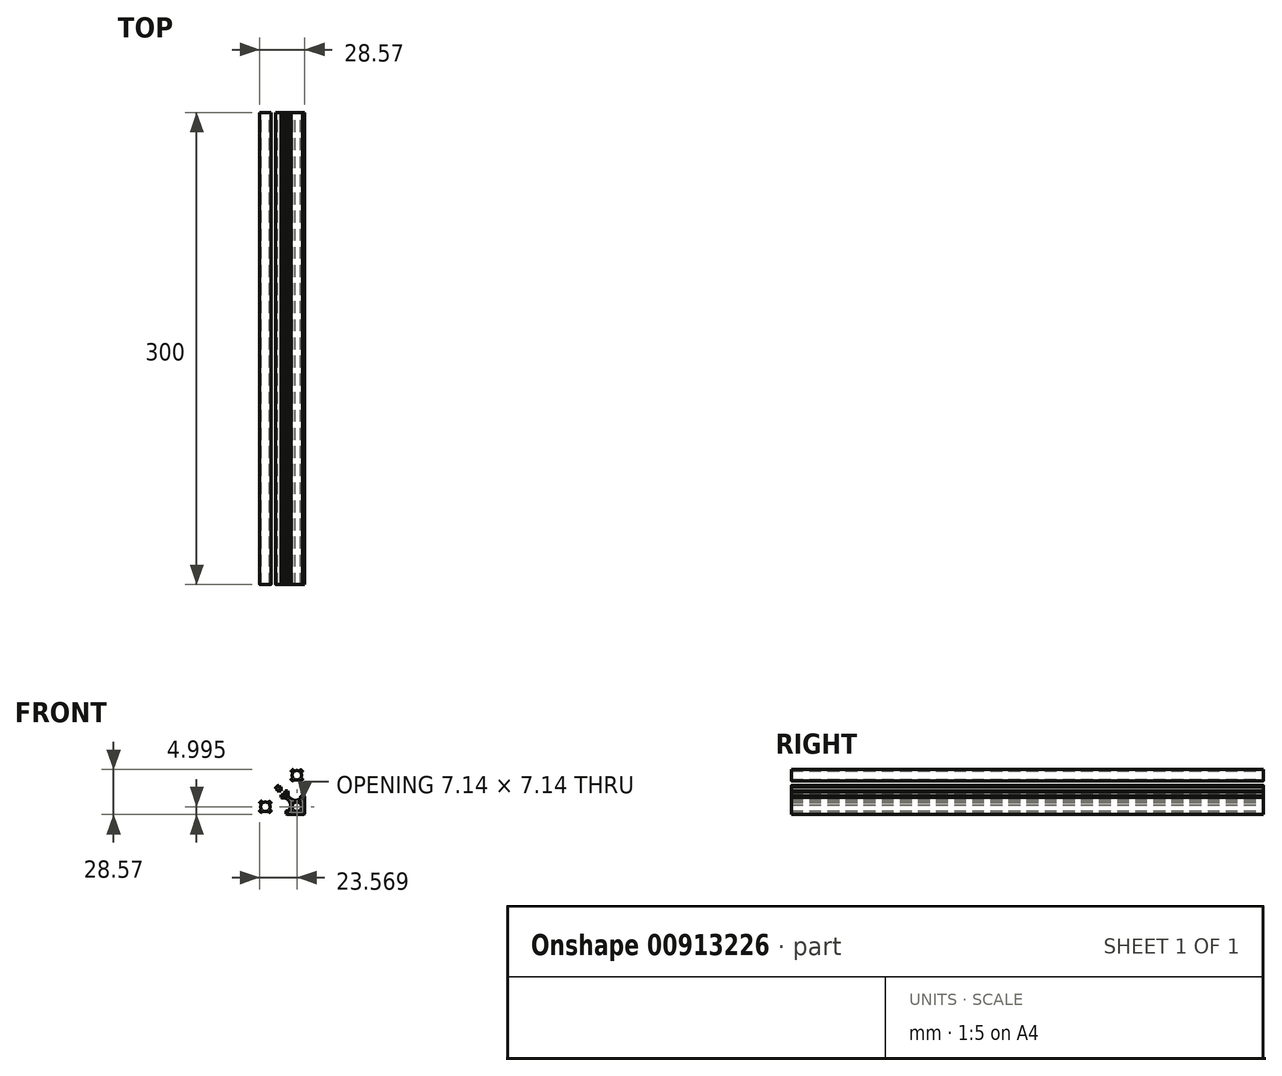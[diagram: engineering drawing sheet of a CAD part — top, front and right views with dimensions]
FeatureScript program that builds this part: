
annotation { "Feature Type Name" : "Feature", "Feature Type Description" : "" }
export const myFeature = defineFeature(function(context is Context, id is Id, definition is map)
    precondition{}
    {
        {
            var Q0;
            Q0=qCreatedBy(makeId("Front.planeOp"),FACE);
            var sketch = newSketch(context, id + "F0", { "sketchPlane" : qUnion([Q0])});
            skLineSegment(sketch, "E0", {"start": v(-2.82, -20.25) * mm, "end": v(-2.82, -15.85) * mm});
            skLineSegment(sketch, "E1", {"start": v(-5.02, -18.05) * mm, "end": v(-0.62, -18.05) * mm});
            skArc(sketch, "E2", {"start": v(-5.5, -19.39) * mm, "mid": v(-5.48, -19.57) * mm, "end": v(-5.56, -19.74) * mm});
            skLineSegment(sketch, "E3", {"start": v(-5.56, -19.74) * mm, "end": v(-6.3, -20.48) * mm});
            skArc(sketch, "E4", {"start": v(-6.3, -20.48) * mm, "mid": v(-6.4, -20.67) * mm, "end": v(-6.32, -20.88) * mm});
            skArc(sketch, "E5", {"start": v(-6.32, -20.88) * mm, "mid": v(-6, -21.24) * mm, "end": v(-5.64, -21.56) * mm});
            skArc(sketch, "E6", {"start": v(-5.64, -21.56) * mm, "mid": v(-5.44, -21.62) * mm, "end": v(-5.24, -21.54) * mm});
            skLineSegment(sketch, "E7", {"start": v(-5.24, -21.54) * mm, "end": v(-4.5, -20.8) * mm});
            skArc(sketch, "E8", {"start": v(-4.5, -20.8) * mm, "mid": v(-4.34, -20.71) * mm, "end": v(-4.16, -20.74) * mm});
            skArc(sketch, "E9", {"start": v(-4.16, -20.74) * mm, "mid": v(-2.82, -21.05) * mm, "end": v(-1.48, -20.74) * mm});
            skArc(sketch, "E10", {"start": v(-1.48, -20.74) * mm, "mid": v(-1.3, -20.71) * mm, "end": v(-1.14, -20.8) * mm});
            skLineSegment(sketch, "E11", {"start": v(-1.14, -20.8) * mm, "end": v(-0.4, -21.54) * mm});
            skArc(sketch, "E12", {"start": v(-0.4, -21.54) * mm, "mid": v(-0.2, -21.62) * mm, "end": v(0, -21.56) * mm});
            skArc(sketch, "E13", {"start": v(0, -21.56) * mm, "mid": v(0.36, -21.24) * mm, "end": v(0.68, -20.88) * mm});
            skArc(sketch, "E14", {"start": v(0.68, -20.88) * mm, "mid": v(0.75, -20.67) * mm, "end": v(0.66, -20.48) * mm});
            skLineSegment(sketch, "E15", {"start": v(0.66, -20.48) * mm, "end": v(-0.08, -19.74) * mm});
            skArc(sketch, "E16", {"start": v(-0.08, -19.74) * mm, "mid": v(-0.16, -19.57) * mm, "end": v(-0.13, -19.39) * mm});
            skArc(sketch, "E17", {"start": v(-0.13, -19.39) * mm, "mid": v(0.18, -18.05) * mm, "end": v(-0.13, -16.72) * mm});
            skArc(sketch, "E18", {"start": v(-0.13, -16.72) * mm, "mid": v(-0.16, -16.54) * mm, "end": v(-0.08, -16.37) * mm});
            skLineSegment(sketch, "E19", {"start": v(-0.08, -16.37) * mm, "end": v(0.66, -15.63) * mm});
            skArc(sketch, "E20", {"start": v(0.66, -15.63) * mm, "mid": v(0.75, -15.44) * mm, "end": v(0.68, -15.23) * mm});
            skArc(sketch, "E21", {"start": v(0.68, -15.23) * mm, "mid": v(0.36, -14.87) * mm, "end": v(0, -14.55) * mm});
            skArc(sketch, "E22", {"start": v(0, -14.55) * mm, "mid": v(-0.2, -14.48) * mm, "end": v(-0.4, -14.57) * mm});
            skLineSegment(sketch, "E23", {"start": v(-0.4, -14.57) * mm, "end": v(-1.14, -15.31) * mm});
            skArc(sketch, "E24", {"start": v(-1.14, -15.31) * mm, "mid": v(-1.3, -15.4) * mm, "end": v(-1.48, -15.37) * mm});
            skArc(sketch, "E25", {"start": v(-1.48, -15.37) * mm, "mid": v(-2.82, -15.05) * mm, "end": v(-4.16, -15.37) * mm});
            skArc(sketch, "E26", {"start": v(-4.16, -15.37) * mm, "mid": v(-4.34, -15.4) * mm, "end": v(-4.5, -15.31) * mm});
            skLineSegment(sketch, "E27", {"start": v(-4.5, -15.31) * mm, "end": v(-5.24, -14.57) * mm});
            skArc(sketch, "E28", {"start": v(-5.24, -14.57) * mm, "mid": v(-5.44, -14.48) * mm, "end": v(-5.64, -14.55) * mm});
            skArc(sketch, "E29", {"start": v(-5.64, -14.55) * mm, "mid": v(-6, -14.87) * mm, "end": v(-6.32, -15.23) * mm});
            skArc(sketch, "E30", {"start": v(-6.32, -15.23) * mm, "mid": v(-6.4, -15.44) * mm, "end": v(-6.3, -15.63) * mm});
            skLineSegment(sketch, "E31", {"start": v(-6.3, -15.63) * mm, "end": v(-5.56, -16.37) * mm});
            skArc(sketch, "E32", {"start": v(-5.56, -16.37) * mm, "mid": v(-5.48, -16.54) * mm, "end": v(-5.5, -16.72) * mm});
            skArc(sketch, "E33", {"start": v(-5.5, -16.72) * mm, "mid": v(-5.82, -18.05) * mm, "end": v(-5.5, -19.39) * mm});
            skLineSegment(sketch, "E34", {"start": v(-5.02, -38.05) * mm, "end": v(-0.62, -38.05) * mm});
            skLineSegment(sketch, "E35", {"start": v(-2.82, -35.85) * mm, "end": v(-2.82, -40.25) * mm});
            skArc(sketch, "E36", {"start": v(-5.5, -36.72) * mm, "mid": v(-5.48, -36.54) * mm, "end": v(-5.56, -36.37) * mm});
            skLineSegment(sketch, "E37", {"start": v(-5.56, -36.37) * mm, "end": v(-6.3, -35.63) * mm});
            skArc(sketch, "E38", {"start": v(-6.3, -35.63) * mm, "mid": v(-6.4, -35.44) * mm, "end": v(-6.33, -35.23) * mm});
            skArc(sketch, "E39", {"start": v(-6.33, -35.23) * mm, "mid": v(-6, -34.87) * mm, "end": v(-5.64, -34.55) * mm});
            skArc(sketch, "E40", {"start": v(-5.64, -34.55) * mm, "mid": v(-5.44, -34.48) * mm, "end": v(-5.24, -34.57) * mm});
            skLineSegment(sketch, "E41", {"start": v(-5.24, -34.57) * mm, "end": v(-4.5, -35.31) * mm});
            skArc(sketch, "E42", {"start": v(-4.5, -35.31) * mm, "mid": v(-4.34, -35.4) * mm, "end": v(-4.16, -35.37) * mm});
            skArc(sketch, "E43", {"start": v(-4.16, -35.37) * mm, "mid": v(-2.82, -35.05) * mm, "end": v(-1.48, -35.37) * mm});
            skArc(sketch, "E44", {"start": v(-1.48, -35.37) * mm, "mid": v(-1.3, -35.4) * mm, "end": v(-1.14, -35.31) * mm});
            skLineSegment(sketch, "E45", {"start": v(-1.14, -35.31) * mm, "end": v(-0.4, -34.57) * mm});
            skArc(sketch, "E46", {"start": v(-0.4, -34.57) * mm, "mid": v(-0.2, -34.48) * mm, "end": v(0, -34.55) * mm});
            skArc(sketch, "E47", {"start": v(0, -34.55) * mm, "mid": v(0.36, -34.87) * mm, "end": v(0.68, -35.23) * mm});
            skArc(sketch, "E48", {"start": v(0.68, -35.23) * mm, "mid": v(0.75, -35.44) * mm, "end": v(0.66, -35.63) * mm});
            skLineSegment(sketch, "E49", {"start": v(0.66, -35.63) * mm, "end": v(-0.08, -36.37) * mm});
            skArc(sketch, "E50", {"start": v(-0.08, -36.37) * mm, "mid": v(-0.16, -36.54) * mm, "end": v(-0.13, -36.72) * mm});
            skArc(sketch, "E51", {"start": v(-0.13, -36.72) * mm, "mid": v(0.18, -38.05) * mm, "end": v(-0.14, -39.4) * mm});
            skArc(sketch, "E52", {"start": v(-0.14, -39.4) * mm, "mid": v(-0.16, -39.57) * mm, "end": v(-0.08, -39.74) * mm});
            skLineSegment(sketch, "E53", {"start": v(-0.08, -39.74) * mm, "end": v(0.66, -40.48) * mm});
            skArc(sketch, "E54", {"start": v(0.66, -40.48) * mm, "mid": v(0.75, -40.67) * mm, "end": v(0.68, -40.88) * mm});
            skArc(sketch, "E55", {"start": v(0.68, -40.88) * mm, "mid": v(0.36, -41.24) * mm, "end": v(0, -41.56) * mm});
            skArc(sketch, "E56", {"start": v(0, -41.56) * mm, "mid": v(-0.2, -41.63) * mm, "end": v(-0.4, -41.54) * mm});
            skLineSegment(sketch, "E57", {"start": v(-0.4, -41.54) * mm, "end": v(-1.14, -40.8) * mm});
            skArc(sketch, "E58", {"start": v(-1.14, -40.8) * mm, "mid": v(-1.3, -40.71) * mm, "end": v(-1.49, -40.74) * mm});
            skArc(sketch, "E59", {"start": v(-1.49, -40.74) * mm, "mid": v(-2.82, -41.05) * mm, "end": v(-4.16, -40.74) * mm});
            skArc(sketch, "E60", {"start": v(-4.16, -40.74) * mm, "mid": v(-4.34, -40.71) * mm, "end": v(-4.5, -40.8) * mm});
            skLineSegment(sketch, "E61", {"start": v(-4.5, -40.8) * mm, "end": v(-5.24, -41.54) * mm});
            skArc(sketch, "E62", {"start": v(-5.24, -41.54) * mm, "mid": v(-5.44, -41.62) * mm, "end": v(-5.64, -41.56) * mm});
            skArc(sketch, "E63", {"start": v(-5.64, -41.56) * mm, "mid": v(-6, -41.24) * mm, "end": v(-6.33, -40.88) * mm});
            skArc(sketch, "E64", {"start": v(-6.33, -40.88) * mm, "mid": v(-6.4, -40.67) * mm, "end": v(-6.3, -40.48) * mm});
            skLineSegment(sketch, "E65", {"start": v(-6.3, -40.48) * mm, "end": v(-5.56, -39.74) * mm});
            skArc(sketch, "E66", {"start": v(-5.56, -39.74) * mm, "mid": v(-5.48, -39.57) * mm, "end": v(-5.5, -39.4) * mm});
            skArc(sketch, "E67", {"start": v(-5.5, -39.4) * mm, "mid": v(-5.82, -38.05) * mm, "end": v(-5.5, -36.72) * mm});
            skArc(sketch, "E68", {"start": v(-20.13, -36.72) * mm, "mid": v(-20.16, -36.54) * mm, "end": v(-20.07, -36.37) * mm});
            skLineSegment(sketch, "E69", {"start": v(-20.07, -36.37) * mm, "end": v(-19.33, -35.63) * mm});
            skArc(sketch, "E70", {"start": v(-19.33, -35.63) * mm, "mid": v(-19.25, -35.44) * mm, "end": v(-19.31, -35.23) * mm});
            skArc(sketch, "E71", {"start": v(-19.31, -35.23) * mm, "mid": v(-19.64, -34.87) * mm, "end": v(-20, -34.55) * mm});
            skArc(sketch, "E72", {"start": v(-20, -34.55) * mm, "mid": v(-20.2, -34.48) * mm, "end": v(-20.4, -34.57) * mm});
            skLineSegment(sketch, "E73", {"start": v(-20.4, -34.57) * mm, "end": v(-21.14, -35.31) * mm});
            skArc(sketch, "E74", {"start": v(-21.14, -35.31) * mm, "mid": v(-21.3, -35.4) * mm, "end": v(-21.48, -35.37) * mm});
            skArc(sketch, "E75", {"start": v(-21.48, -35.37) * mm, "mid": v(-22.82, -35.05) * mm, "end": v(-24.15, -35.37) * mm});
            skArc(sketch, "E76", {"start": v(-24.15, -35.37) * mm, "mid": v(-24.34, -35.4) * mm, "end": v(-24.5, -35.31) * mm});
            skLineSegment(sketch, "E77", {"start": v(-24.5, -35.31) * mm, "end": v(-25.24, -34.57) * mm});
            skArc(sketch, "E78", {"start": v(-25.24, -34.57) * mm, "mid": v(-25.44, -34.48) * mm, "end": v(-25.64, -34.55) * mm});
            skArc(sketch, "E79", {"start": v(-25.64, -34.55) * mm, "mid": v(-26, -34.87) * mm, "end": v(-26.32, -35.23) * mm});
            skArc(sketch, "E80", {"start": v(-26.32, -35.23) * mm, "mid": v(-26.39, -35.44) * mm, "end": v(-26.3, -35.63) * mm});
            skLineSegment(sketch, "E81", {"start": v(-26.3, -35.63) * mm, "end": v(-25.56, -36.37) * mm});
            skArc(sketch, "E82", {"start": v(-25.56, -36.37) * mm, "mid": v(-25.48, -36.54) * mm, "end": v(-25.5, -36.72) * mm});
            skArc(sketch, "E83", {"start": v(-25.5, -36.72) * mm, "mid": v(-25.82, -38.05) * mm, "end": v(-25.5, -39.4) * mm});
            skArc(sketch, "E84", {"start": v(-25.5, -39.4) * mm, "mid": v(-25.48, -39.57) * mm, "end": v(-25.56, -39.74) * mm});
            skLineSegment(sketch, "E85", {"start": v(-25.56, -39.74) * mm, "end": v(-26.3, -40.48) * mm});
            skArc(sketch, "E86", {"start": v(-26.3, -40.48) * mm, "mid": v(-26.39, -40.67) * mm, "end": v(-26.32, -40.88) * mm});
            skArc(sketch, "E87", {"start": v(-26.32, -40.88) * mm, "mid": v(-26, -41.24) * mm, "end": v(-25.64, -41.56) * mm});
            skArc(sketch, "E88", {"start": v(-25.64, -41.56) * mm, "mid": v(-25.44, -41.63) * mm, "end": v(-25.24, -41.54) * mm});
            skLineSegment(sketch, "E89", {"start": v(-25.24, -41.54) * mm, "end": v(-24.5, -40.8) * mm});
            skArc(sketch, "E90", {"start": v(-24.5, -40.8) * mm, "mid": v(-24.33, -40.71) * mm, "end": v(-24.15, -40.74) * mm});
            skArc(sketch, "E91", {"start": v(-24.15, -40.74) * mm, "mid": v(-22.82, -41.05) * mm, "end": v(-21.48, -40.74) * mm});
            skArc(sketch, "E92", {"start": v(-21.48, -40.74) * mm, "mid": v(-21.3, -40.71) * mm, "end": v(-21.14, -40.8) * mm});
            skLineSegment(sketch, "E93", {"start": v(-21.14, -40.8) * mm, "end": v(-20.4, -41.54) * mm});
            skArc(sketch, "E94", {"start": v(-20.4, -41.54) * mm, "mid": v(-20.2, -41.62) * mm, "end": v(-20, -41.56) * mm});
            skArc(sketch, "E95", {"start": v(-20, -41.56) * mm, "mid": v(-19.63, -41.24) * mm, "end": v(-19.31, -40.88) * mm});
            skArc(sketch, "E96", {"start": v(-19.31, -40.88) * mm, "mid": v(-19.25, -40.67) * mm, "end": v(-19.33, -40.48) * mm});
            skLineSegment(sketch, "E97", {"start": v(-19.33, -40.48) * mm, "end": v(-20.07, -39.74) * mm});
            skArc(sketch, "E98", {"start": v(-20.07, -39.74) * mm, "mid": v(-20.16, -39.57) * mm, "end": v(-20.13, -39.4) * mm});
            skArc(sketch, "E99", {"start": v(-20.13, -39.4) * mm, "mid": v(-19.82, -38.05) * mm, "end": v(-20.13, -36.72) * mm});
            skLineSegment(sketch, "E100", {"start": v(-22.82, -35.85) * mm, "end": v(-22.82, -40.25) * mm});
            skLineSegment(sketch, "E101", {"start": v(-20.62, -38.05) * mm, "end": v(-25.02, -38.05) * mm});
            skLineSegment(sketch, "E102", {"start": v(-20.62, -18.05) * mm, "end": v(-25.02, -18.05) * mm});
            skLineSegment(sketch, "E103", {"start": v(-22.82, -20.25) * mm, "end": v(-22.82, -15.85) * mm});
            skLineSegment(sketch, "E104", {"start": v(2.64, -28.05) * mm, "end": v(-29.04, -28.05) * mm});
            skLineSegment(sketch, "E105", {"start": v(-12.82, -44) * mm, "end": v(-12.82, -12.06) * mm});
            skArc(sketch, "E106", {"start": v(-9.58, -26.47) * mm, "mid": v(-9.36, -26.3) * mm, "end": v(-9.38, -26.02) * mm});
            skArc(sketch, "E107", {"start": v(-9.38, -26.02) * mm, "mid": v(-10, -25.23) * mm, "end": v(-10.78, -24.61) * mm});
            skArc(sketch, "E108", {"start": v(-10.78, -24.61) * mm, "mid": v(-11.06, -24.6) * mm, "end": v(-11.23, -24.82) * mm});
            skLineSegment(sketch, "E109", {"start": v(-11.23, -24.82) * mm, "end": v(-11.37, -25.56) * mm});
            skArc(sketch, "E110", {"start": v(-11.37, -25.56) * mm, "mid": v(-11.52, -25.77) * mm, "end": v(-11.78, -25.78) * mm});
            skArc(sketch, "E111", {"start": v(-11.78, -25.78) * mm, "mid": v(-12.82, -25.55) * mm, "end": v(-13.85, -25.78) * mm});
            skArc(sketch, "E112", {"start": v(-13.85, -25.78) * mm, "mid": v(-14.11, -25.77) * mm, "end": v(-14.27, -25.56) * mm});
            skLineSegment(sketch, "E113", {"start": v(-14.27, -25.56) * mm, "end": v(-14.4, -24.82) * mm});
            skArc(sketch, "E114", {"start": v(-14.4, -24.82) * mm, "mid": v(-14.57, -24.6) * mm, "end": v(-14.85, -24.61) * mm});
            skArc(sketch, "E115", {"start": v(-14.85, -24.61) * mm, "mid": v(-15.65, -25.23) * mm, "end": v(-16.26, -26.02) * mm});
            skArc(sketch, "E116", {"start": v(-16.26, -26.02) * mm, "mid": v(-16.27, -26.3) * mm, "end": v(-16.06, -26.47) * mm});
            skLineSegment(sketch, "E117", {"start": v(-16.06, -26.47) * mm, "end": v(-15.31, -26.6) * mm});
            skArc(sketch, "E118", {"start": v(-15.31, -26.6) * mm, "mid": v(-15.1, -26.76) * mm, "end": v(-15.1, -27.02) * mm});
            skArc(sketch, "E119", {"start": v(-15.1, -27.02) * mm, "mid": v(-15.32, -28.05) * mm, "end": v(-15.1, -29.09) * mm});
            skArc(sketch, "E120", {"start": v(-15.1, -29.09) * mm, "mid": v(-15.1, -29.35) * mm, "end": v(-15.31, -29.5) * mm});
            skLineSegment(sketch, "E121", {"start": v(-15.31, -29.5) * mm, "end": v(-16.06, -29.64) * mm});
            skArc(sketch, "E122", {"start": v(-16.06, -29.64) * mm, "mid": v(-16.27, -29.81) * mm, "end": v(-16.26, -30.09) * mm});
            skArc(sketch, "E123", {"start": v(-16.26, -30.09) * mm, "mid": v(-15.65, -30.88) * mm, "end": v(-14.85, -31.5) * mm});
            skArc(sketch, "E124", {"start": v(-14.85, -31.5) * mm, "mid": v(-14.57, -31.51) * mm, "end": v(-14.4, -31.3) * mm});
            skLineSegment(sketch, "E125", {"start": v(-14.4, -31.3) * mm, "end": v(-14.27, -30.55) * mm});
            skArc(sketch, "E126", {"start": v(-14.27, -30.55) * mm, "mid": v(-14.11, -30.34) * mm, "end": v(-13.85, -30.33) * mm});
            skArc(sketch, "E127", {"start": v(-13.85, -30.33) * mm, "mid": v(-12.82, -30.55) * mm, "end": v(-11.78, -30.33) * mm});
            skArc(sketch, "E128", {"start": v(-11.78, -30.33) * mm, "mid": v(-11.52, -30.34) * mm, "end": v(-11.37, -30.55) * mm});
            skLineSegment(sketch, "E129", {"start": v(-11.37, -30.55) * mm, "end": v(-11.23, -31.3) * mm});
            skArc(sketch, "E130", {"start": v(-11.23, -31.3) * mm, "mid": v(-11.06, -31.51) * mm, "end": v(-10.78, -31.5) * mm});
            skArc(sketch, "E131", {"start": v(-10.78, -31.5) * mm, "mid": v(-10, -30.88) * mm, "end": v(-9.38, -30.09) * mm});
            skArc(sketch, "E132", {"start": v(-9.38, -30.09) * mm, "mid": v(-9.36, -29.81) * mm, "end": v(-9.58, -29.64) * mm});
            skLineSegment(sketch, "E133", {"start": v(-9.58, -29.64) * mm, "end": v(-10.32, -29.5) * mm});
            skArc(sketch, "E134", {"start": v(-10.32, -29.5) * mm, "mid": v(-10.53, -29.35) * mm, "end": v(-10.54, -29.09) * mm});
            skArc(sketch, "E135", {"start": v(-10.54, -29.09) * mm, "mid": v(-10.32, -28.05) * mm, "end": v(-10.54, -27.02) * mm});
            skArc(sketch, "E136", {"start": v(-10.54, -27.02) * mm, "mid": v(-10.53, -26.76) * mm, "end": v(-10.32, -26.6) * mm});
            skLineSegment(sketch, "E137", {"start": v(-10.32, -26.6) * mm, "end": v(-9.58, -26.47) * mm});
            skArc(sketch, "E138", {"start": v(-20.13, -19.39) * mm, "mid": v(-20.16, -19.57) * mm, "end": v(-20.08, -19.74) * mm});
            skLineSegment(sketch, "E139", {"start": v(-20.08, -19.74) * mm, "end": v(-19.33, -20.48) * mm});
            skArc(sketch, "E140", {"start": v(-19.33, -20.48) * mm, "mid": v(-19.25, -20.67) * mm, "end": v(-19.31, -20.88) * mm});
            skArc(sketch, "E141", {"start": v(-19.31, -20.88) * mm, "mid": v(-19.64, -21.24) * mm, "end": v(-20, -21.56) * mm});
            skArc(sketch, "E142", {"start": v(-20, -21.56) * mm, "mid": v(-20.2, -21.62) * mm, "end": v(-20.4, -21.54) * mm});
            skLineSegment(sketch, "E143", {"start": v(-20.4, -21.54) * mm, "end": v(-21.14, -20.8) * mm});
            skArc(sketch, "E144", {"start": v(-21.14, -20.8) * mm, "mid": v(-21.3, -20.71) * mm, "end": v(-21.48, -20.74) * mm});
            skArc(sketch, "E145", {"start": v(-21.48, -20.74) * mm, "mid": v(-22.82, -21.05) * mm, "end": v(-24.15, -20.74) * mm});
            skArc(sketch, "E146", {"start": v(-24.15, -20.74) * mm, "mid": v(-24.34, -20.71) * mm, "end": v(-24.5, -20.8) * mm});
            skLineSegment(sketch, "E147", {"start": v(-24.5, -20.8) * mm, "end": v(-25.24, -21.54) * mm});
            skArc(sketch, "E148", {"start": v(-25.24, -21.54) * mm, "mid": v(-25.44, -21.62) * mm, "end": v(-25.64, -21.56) * mm});
            skArc(sketch, "E149", {"start": v(-25.64, -21.56) * mm, "mid": v(-26, -21.24) * mm, "end": v(-26.32, -20.88) * mm});
            skArc(sketch, "E150", {"start": v(-26.32, -20.88) * mm, "mid": v(-26.39, -20.67) * mm, "end": v(-26.3, -20.48) * mm});
            skLineSegment(sketch, "E151", {"start": v(-26.3, -20.48) * mm, "end": v(-25.56, -19.74) * mm});
            skArc(sketch, "E152", {"start": v(-25.56, -19.74) * mm, "mid": v(-25.48, -19.57) * mm, "end": v(-25.5, -19.39) * mm});
            skArc(sketch, "E153", {"start": v(-25.5, -19.39) * mm, "mid": v(-25.82, -18.05) * mm, "end": v(-25.5, -16.72) * mm});
            skArc(sketch, "E154", {"start": v(-25.5, -16.72) * mm, "mid": v(-25.48, -16.54) * mm, "end": v(-25.56, -16.37) * mm});
            skLineSegment(sketch, "E155", {"start": v(-25.56, -16.37) * mm, "end": v(-26.3, -15.63) * mm});
            skArc(sketch, "E156", {"start": v(-26.3, -15.63) * mm, "mid": v(-26.39, -15.44) * mm, "end": v(-26.32, -15.23) * mm});
            skArc(sketch, "E157", {"start": v(-26.32, -15.23) * mm, "mid": v(-26, -14.87) * mm, "end": v(-25.64, -14.55) * mm});
            skArc(sketch, "E158", {"start": v(-25.64, -14.55) * mm, "mid": v(-25.44, -14.48) * mm, "end": v(-25.24, -14.57) * mm});
            skLineSegment(sketch, "E159", {"start": v(-25.24, -14.57) * mm, "end": v(-24.5, -15.31) * mm});
            skArc(sketch, "E160", {"start": v(-24.5, -15.31) * mm, "mid": v(-24.34, -15.4) * mm, "end": v(-24.15, -15.37) * mm});
            skArc(sketch, "E161", {"start": v(-24.15, -15.37) * mm, "mid": v(-22.82, -15.05) * mm, "end": v(-21.48, -15.37) * mm});
            skArc(sketch, "E162", {"start": v(-21.48, -15.37) * mm, "mid": v(-21.3, -15.4) * mm, "end": v(-21.14, -15.31) * mm});
            skLineSegment(sketch, "E163", {"start": v(-21.14, -15.31) * mm, "end": v(-20.4, -14.57) * mm});
            skArc(sketch, "E164", {"start": v(-20.4, -14.57) * mm, "mid": v(-20.2, -14.48) * mm, "end": v(-20, -14.55) * mm});
            skArc(sketch, "E165", {"start": v(-20, -14.55) * mm, "mid": v(-19.64, -14.87) * mm, "end": v(-19.31, -15.23) * mm});
            skArc(sketch, "E166", {"start": v(-19.31, -15.23) * mm, "mid": v(-19.25, -15.44) * mm, "end": v(-19.33, -15.63) * mm});
            skLineSegment(sketch, "E167", {"start": v(-19.33, -15.63) * mm, "end": v(-20.08, -16.37) * mm});
            skArc(sketch, "E168", {"start": v(-20.08, -16.37) * mm, "mid": v(-20.16, -16.54) * mm, "end": v(-20.13, -16.72) * mm});
            skArc(sketch, "E169", {"start": v(-20.13, -16.72) * mm, "mid": v(-19.82, -18.05) * mm, "end": v(-20.13, -19.39) * mm});
            skLineSegment(sketch, "E170", {"start": v(-8.87, -43.05) * mm, "end": v(-9.67, -42.55) * mm});
            skLineSegment(sketch, "E171", {"start": v(-9.67, -42.55) * mm, "end": v(-9.67, -40.85) * mm});
            skArc(sketch, "E172", {"start": v(-9.67, -40.85) * mm, "mid": v(-9.58, -40.64) * mm, "end": v(-9.37, -40.55) * mm});
            skLineSegment(sketch, "E173", {"start": v(-9.37, -40.55) * mm, "end": v(-7.72, -40.55) * mm});
            skLineSegment(sketch, "E174", {"start": v(-7.72, -40.55) * mm, "end": v(-6.73, -37.5) * mm});
            skArc(sketch, "E175", {"start": v(-6.73, -37.5) * mm, "mid": v(-6.68, -37.24) * mm, "end": v(-6.7, -36.98) * mm});
            skArc(sketch, "E176", {"start": v(-6.7, -36.98) * mm, "mid": v(-7.54, -34.94) * mm, "end": v(-8.81, -33.14) * mm});
            skArc(sketch, "E177", {"start": v(-8.81, -33.14) * mm, "mid": v(-9.66, -32.7) * mm, "end": v(-10.6, -32.55) * mm});
            skLineSegment(sketch, "E178", {"start": v(-10.6, -32.55) * mm, "end": v(-12.32, -32.55) * mm});
            skLineSegment(sketch, "E179", {"start": v(-12.32, -32.55) * mm, "end": v(-12.82, -32.05) * mm});
            skLineSegment(sketch, "E180", {"start": v(-12.82, -32.05) * mm, "end": v(-13.32, -32.55) * mm});
            skLineSegment(sketch, "E181", {"start": v(-13.32, -32.55) * mm, "end": v(-15.04, -32.55) * mm});
            skArc(sketch, "E182", {"start": v(-15.04, -32.55) * mm, "mid": v(-15.98, -32.7) * mm, "end": v(-16.82, -33.14) * mm});
            skArc(sketch, "E183", {"start": v(-16.82, -33.14) * mm, "mid": v(-18.1, -34.94) * mm, "end": v(-18.93, -36.98) * mm});
            skArc(sketch, "E184", {"start": v(-18.93, -36.98) * mm, "mid": v(-18.95, -37.24) * mm, "end": v(-18.9, -37.5) * mm});
            skLineSegment(sketch, "E185", {"start": v(-18.9, -37.5) * mm, "end": v(-17.92, -40.55) * mm});
            skLineSegment(sketch, "E186", {"start": v(-17.92, -40.55) * mm, "end": v(-16.27, -40.55) * mm});
            skArc(sketch, "E187", {"start": v(-16.27, -40.55) * mm, "mid": v(-16.06, -40.64) * mm, "end": v(-15.97, -40.85) * mm});
            skLineSegment(sketch, "E188", {"start": v(-15.97, -40.85) * mm, "end": v(-15.97, -42.55) * mm});
            skLineSegment(sketch, "E189", {"start": v(-15.97, -42.55) * mm, "end": v(-16.77, -43.05) * mm});
            skLineSegment(sketch, "E190", {"start": v(-16.77, -43.05) * mm, "end": v(-26.82, -43.05) * mm});
            skArc(sketch, "E191", {"start": v(-26.82, -43.05) * mm, "mid": v(-27.52, -42.76) * mm, "end": v(-27.82, -42.05) * mm});
            skLineSegment(sketch, "E192", {"start": v(-27.82, -42.05) * mm, "end": v(-27.82, -32) * mm});
            skLineSegment(sketch, "E193", {"start": v(-27.82, -32) * mm, "end": v(-27.32, -31.2) * mm});
            skLineSegment(sketch, "E194", {"start": v(-27.32, -31.2) * mm, "end": v(-25.62, -31.2) * mm});
            skArc(sketch, "E195", {"start": v(-25.62, -31.2) * mm, "mid": v(-25.4, -31.3) * mm, "end": v(-25.32, -31.5) * mm});
            skLineSegment(sketch, "E196", {"start": v(-25.32, -31.5) * mm, "end": v(-25.32, -33.15) * mm});
            skLineSegment(sketch, "E197", {"start": v(-25.32, -33.15) * mm, "end": v(-22.27, -34.14) * mm});
            skArc(sketch, "E198", {"start": v(-22.27, -34.14) * mm, "mid": v(-22, -34.19) * mm, "end": v(-21.75, -34.17) * mm});
            skArc(sketch, "E199", {"start": v(-21.75, -34.17) * mm, "mid": v(-19.7, -33.33) * mm, "end": v(-17.9, -32.06) * mm});
            skArc(sketch, "E200", {"start": v(-17.9, -32.06) * mm, "mid": v(-17.47, -31.21) * mm, "end": v(-17.32, -30.27) * mm});
            skLineSegment(sketch, "E201", {"start": v(-17.32, -30.27) * mm, "end": v(-17.32, -28.55) * mm});
            skLineSegment(sketch, "E202", {"start": v(-17.32, -28.55) * mm, "end": v(-16.82, -28.05) * mm});
            skLineSegment(sketch, "E203", {"start": v(-16.82, -28.05) * mm, "end": v(-17.32, -27.55) * mm});
            skLineSegment(sketch, "E204", {"start": v(-17.32, -27.55) * mm, "end": v(-17.32, -25.84) * mm});
            skArc(sketch, "E205", {"start": v(-17.32, -25.84) * mm, "mid": v(-17.47, -24.9) * mm, "end": v(-17.9, -24.05) * mm});
            skArc(sketch, "E206", {"start": v(-17.9, -24.05) * mm, "mid": v(-19.7, -22.78) * mm, "end": v(-21.75, -21.94) * mm});
            skArc(sketch, "E207", {"start": v(-21.75, -21.94) * mm, "mid": v(-22, -21.92) * mm, "end": v(-22.27, -21.97) * mm});
            skLineSegment(sketch, "E208", {"start": v(-22.27, -21.97) * mm, "end": v(-25.32, -22.95) * mm});
            skLineSegment(sketch, "E209", {"start": v(-25.32, -22.95) * mm, "end": v(-25.32, -24.6) * mm});
            skArc(sketch, "E210", {"start": v(-25.32, -24.6) * mm, "mid": v(-25.4, -24.82) * mm, "end": v(-25.62, -24.9) * mm});
            skLineSegment(sketch, "E211", {"start": v(-25.62, -24.9) * mm, "end": v(-27.32, -24.9) * mm});
            skLineSegment(sketch, "E212", {"start": v(-27.32, -24.9) * mm, "end": v(-27.82, -24.1) * mm});
            skLineSegment(sketch, "E213", {"start": v(-27.82, -24.1) * mm, "end": v(-27.82, -14.05) * mm});
            skArc(sketch, "E214", {"start": v(-27.82, -14.05) * mm, "mid": v(-27.52, -13.35) * mm, "end": v(-26.82, -13.05) * mm});
            skLineSegment(sketch, "E215", {"start": v(-26.82, -13.05) * mm, "end": v(-16.77, -13.05) * mm});
            skLineSegment(sketch, "E216", {"start": v(-16.77, -13.05) * mm, "end": v(-15.97, -13.55) * mm});
            skLineSegment(sketch, "E217", {"start": v(-15.97, -13.55) * mm, "end": v(-15.97, -15.25) * mm});
            skArc(sketch, "E218", {"start": v(-15.97, -15.25) * mm, "mid": v(-16.06, -15.47) * mm, "end": v(-16.27, -15.55) * mm});
            skLineSegment(sketch, "E219", {"start": v(-16.27, -15.55) * mm, "end": v(-17.92, -15.55) * mm});
            skLineSegment(sketch, "E220", {"start": v(-17.92, -15.55) * mm, "end": v(-18.9, -18.6) * mm});
            skArc(sketch, "E221", {"start": v(-18.9, -18.6) * mm, "mid": v(-18.95, -18.86) * mm, "end": v(-18.93, -19.13) * mm});
            skArc(sketch, "E222", {"start": v(-18.93, -19.13) * mm, "mid": v(-18.1, -21.16) * mm, "end": v(-16.82, -22.96) * mm});
            skArc(sketch, "E223", {"start": v(-16.82, -22.96) * mm, "mid": v(-15.98, -23.4) * mm, "end": v(-15.04, -23.55) * mm});
            skLineSegment(sketch, "E224", {"start": v(-15.04, -23.55) * mm, "end": v(-13.32, -23.55) * mm});
            skLineSegment(sketch, "E225", {"start": v(-13.32, -23.55) * mm, "end": v(-12.82, -24.05) * mm});
            skLineSegment(sketch, "E226", {"start": v(-12.82, -24.05) * mm, "end": v(-12.32, -23.55) * mm});
            skLineSegment(sketch, "E227", {"start": v(-12.32, -23.55) * mm, "end": v(-10.6, -23.55) * mm});
            skArc(sketch, "E228", {"start": v(-10.6, -23.55) * mm, "mid": v(-9.66, -23.4) * mm, "end": v(-8.81, -22.96) * mm});
            skArc(sketch, "E229", {"start": v(-8.81, -22.96) * mm, "mid": v(-7.54, -21.16) * mm, "end": v(-6.7, -19.13) * mm});
            skArc(sketch, "E230", {"start": v(-6.7, -19.13) * mm, "mid": v(-6.68, -18.86) * mm, "end": v(-6.73, -18.6) * mm});
            skLineSegment(sketch, "E231", {"start": v(-6.73, -18.6) * mm, "end": v(-7.72, -15.55) * mm});
            skLineSegment(sketch, "E232", {"start": v(-7.72, -15.55) * mm, "end": v(-9.37, -15.55) * mm});
            skArc(sketch, "E233", {"start": v(-9.37, -15.55) * mm, "mid": v(-9.58, -15.47) * mm, "end": v(-9.67, -15.25) * mm});
            skLineSegment(sketch, "E234", {"start": v(-9.67, -15.25) * mm, "end": v(-9.67, -13.55) * mm});
            skLineSegment(sketch, "E235", {"start": v(-9.67, -13.55) * mm, "end": v(-8.87, -13.05) * mm});
            skLineSegment(sketch, "E236", {"start": v(-8.87, -13.05) * mm, "end": v(1.18, -13.05) * mm});
            skArc(sketch, "E237", {"start": v(1.18, -13.05) * mm, "mid": v(1.89, -13.35) * mm, "end": v(2.18, -14.05) * mm});
            skLineSegment(sketch, "E238", {"start": v(2.18, -14.05) * mm, "end": v(2.18, -24.1) * mm});
            skLineSegment(sketch, "E239", {"start": v(2.18, -24.1) * mm, "end": v(1.68, -24.9) * mm});
            skLineSegment(sketch, "E240", {"start": v(1.68, -24.9) * mm, "end": v(-0.02, -24.9) * mm});
            skArc(sketch, "E241", {"start": v(-0.02, -24.9) * mm, "mid": v(-0.23, -24.82) * mm, "end": v(-0.32, -24.6) * mm});
            skLineSegment(sketch, "E242", {"start": v(-0.32, -24.6) * mm, "end": v(-0.32, -22.95) * mm});
            skLineSegment(sketch, "E243", {"start": v(-0.32, -22.95) * mm, "end": v(-3.37, -21.97) * mm});
            skArc(sketch, "E244", {"start": v(-3.37, -21.97) * mm, "mid": v(-3.63, -21.92) * mm, "end": v(-3.9, -21.94) * mm});
            skArc(sketch, "E245", {"start": v(-3.9, -21.94) * mm, "mid": v(-5.93, -22.78) * mm, "end": v(-7.73, -24.05) * mm});
            skArc(sketch, "E246", {"start": v(-7.73, -24.05) * mm, "mid": v(-8.17, -24.9) * mm, "end": v(-8.32, -25.84) * mm});
            skLineSegment(sketch, "E247", {"start": v(-8.32, -25.84) * mm, "end": v(-8.32, -27.55) * mm});
            skLineSegment(sketch, "E248", {"start": v(-8.32, -27.55) * mm, "end": v(-8.82, -28.05) * mm});
            skLineSegment(sketch, "E249", {"start": v(-8.82, -28.05) * mm, "end": v(-8.32, -28.55) * mm});
            skLineSegment(sketch, "E250", {"start": v(-8.32, -28.55) * mm, "end": v(-8.32, -30.27) * mm});
            skArc(sketch, "E251", {"start": v(-8.32, -30.27) * mm, "mid": v(-8.17, -31.21) * mm, "end": v(-7.73, -32.06) * mm});
            skArc(sketch, "E252", {"start": v(-7.73, -32.06) * mm, "mid": v(-5.93, -33.33) * mm, "end": v(-3.9, -34.17) * mm});
            skArc(sketch, "E253", {"start": v(-3.9, -34.17) * mm, "mid": v(-3.63, -34.19) * mm, "end": v(-3.37, -34.14) * mm});
            skLineSegment(sketch, "E254", {"start": v(-3.37, -34.14) * mm, "end": v(-0.32, -33.15) * mm});
            skLineSegment(sketch, "E255", {"start": v(-0.32, -33.15) * mm, "end": v(-0.32, -31.5) * mm});
            skArc(sketch, "E256", {"start": v(-0.32, -31.5) * mm, "mid": v(-0.23, -31.3) * mm, "end": v(-0.02, -31.2) * mm});
            skLineSegment(sketch, "E257", {"start": v(-0.02, -31.2) * mm, "end": v(1.68, -31.2) * mm});
            skLineSegment(sketch, "E258", {"start": v(1.68, -31.2) * mm, "end": v(2.18, -32) * mm});
            skLineSegment(sketch, "E259", {"start": v(2.18, -32) * mm, "end": v(2.18, -42.05) * mm});
            skArc(sketch, "E260", {"start": v(2.18, -42.05) * mm, "mid": v(1.89, -42.76) * mm, "end": v(1.18, -43.05) * mm});
            skLineSegment(sketch, "E261", {"start": v(1.18, -43.05) * mm, "end": v(-8.87, -43.05) * mm});
            skSolve(sketch);
        }
        {
            var Q0;
            {var subQ1=sQuery(id+"F0.wireOp",EDGE,"E112");Q0=makeQuery(id+"F0.imprint","IMPRINT",FACE,{"disambiguationData":[TD([[makeQuery(id+"F0.imprint","IMPRINT",EDGE,{"derivedFrom":subQ1}),-1.0]])]});}
            var Q1;
            Q1=makeQuery(id+"F0.imprint","IMPRINT",FACE,{"disambiguationData":[TD([[makeQuery(id+"F0.imprint","IMPRINT",EDGE,{"derivedFrom":sQuery(id+"F0.wireOp",EDGE,"E2")}),-1.0]])]});
            var Q2;
            Q2=makeQuery(id+"F0.imprint","IMPRINT",FACE,{"disambiguationData":[TD([[makeQuery(id+"F0.imprint","IMPRINT",EDGE,{"derivedFrom":sQuery(id+"F0.wireOp",EDGE,"E36")}),1.0]])]});
            var Q3;
            Q3=makeQuery(id+"F0.imprint","IMPRINT",FACE,{"disambiguationData":[TD([[makeQuery(id+"F0.imprint","IMPRINT",EDGE,{"derivedFrom":sQuery(id+"F0.wireOp",EDGE,"E68")}),-1.0]])]});
            extrude(context, id + "F1", {"entities" : qUnion([Q0, Q1, Q2, Q3]), "depth" : 300 * mm, "offsetDistance" : 25 * mm});
        }
    });
